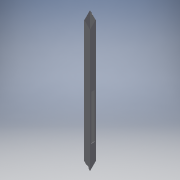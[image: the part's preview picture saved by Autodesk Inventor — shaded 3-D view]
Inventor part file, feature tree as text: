
AUTODESK INVENTOR PART (.ipt)
format: ipt  version: 2016 (Build 200138000, 138)  size: 116,224 bytes
history: native  units: in
note: dims shown in document units (in); Inventor stores cm internally (conversion verified against a paired STEP export)
features: extrude x3, sketch x3
ambient origin geometry x8: Origin, YZ Plane, XZ Plane, XY Plane, X Axis, Y Axis, Z Axis, Center Point
bodies: Solid1 (feature_tree)
feature tree (6):
  extrude  "Extrusion1"  Depth=1.0in
  extrude  "Extrusion2"  Depth=22.75in TaperAngle=0.0deg
  extrude  "Extrusion4"  Depth=1.0in
  sketch  "Sketch1"  dims[d0=1.0in d1=1.0in]
  sketch  "Sketch2"  dims[d2=0.0625in d3=22.75in d4=0.0in]
  sketch  "Sketch4"  dims[d5=0.5in d6=0.5in d7=1.0in d8=0.0in d14=0.5in d15=0.518in d16=0.5in d17=1.0in d18=0.0in]
